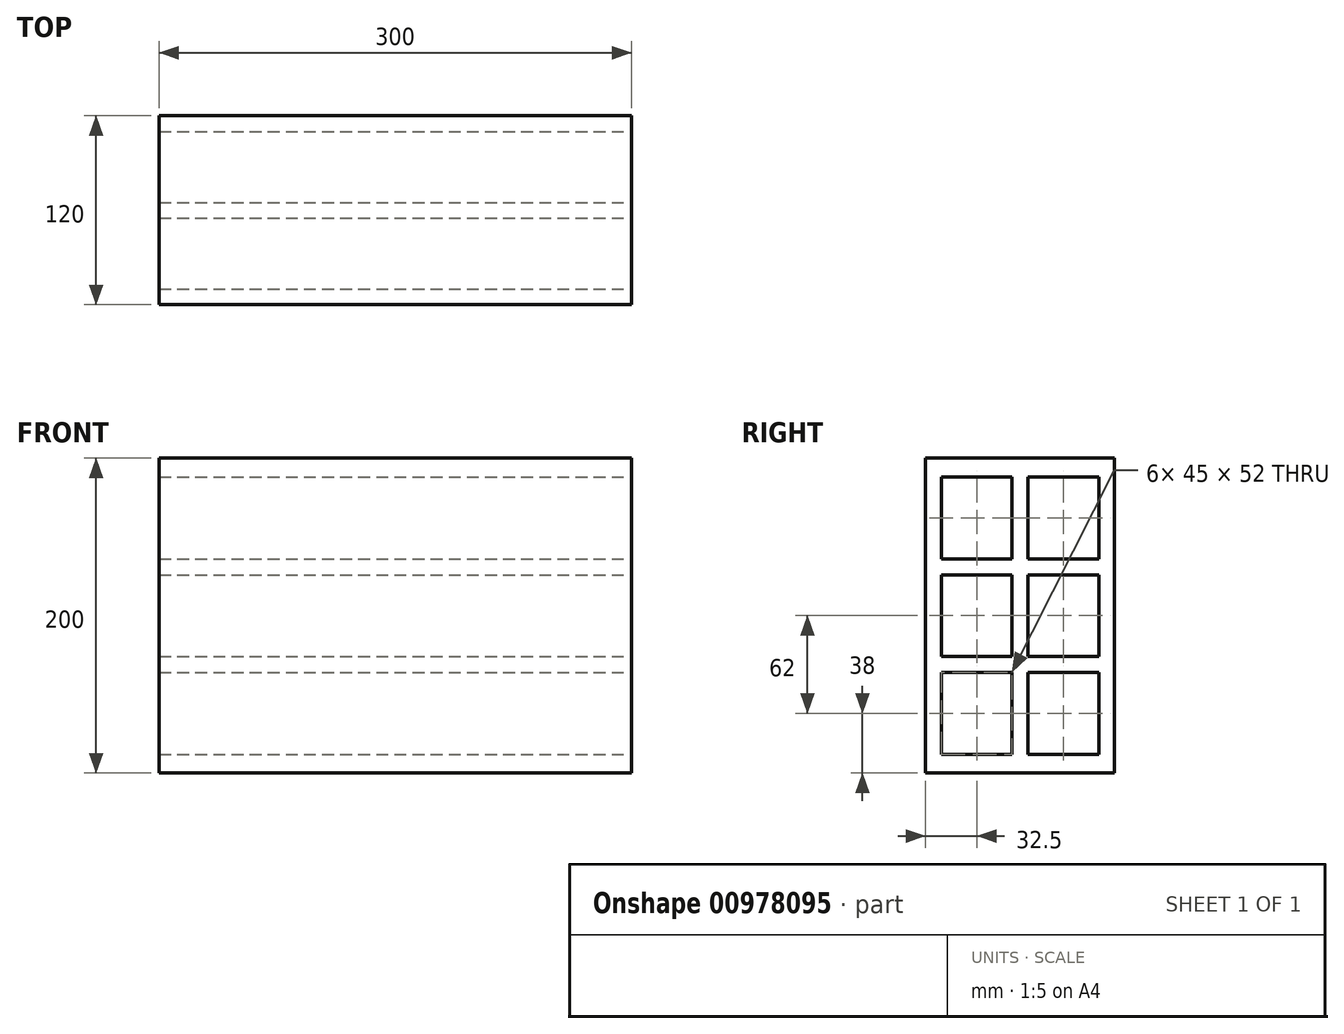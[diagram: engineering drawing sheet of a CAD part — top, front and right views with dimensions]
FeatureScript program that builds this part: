
annotation { "Feature Type Name" : "Feature", "Feature Type Description" : "" }
export const myFeature = defineFeature(function(context is Context, id is Id, definition is map)
    precondition{}
    {
        {
            var Q0;
            Q0=qCreatedBy(makeId("Front.planeOp"),FACE);
            var sketch = newSketch(context, id + "F0", { "sketchPlane" : qUnion([Q0])});
            skLineSegment(sketch, "E0.bottom", {"start": v(-150, 100) * mm, "end": v(150, 100) * mm});
            skLineSegment(sketch, "E0.top", {"start": v(-150, -100) * mm, "end": v(150, -100) * mm});
            skLineSegment(sketch, "E0.left", {"start": v(-150, 100) * mm, "end": v(-150, -100) * mm});
            skLineSegment(sketch, "E0.right", {"start": v(150, 100) * mm, "end": v(150, -100) * mm});
            skPoint(sketch, "E0.middle", {"position": v(0, 0) * mm});
            skSolve(sketch);
        }
        {
            var Q0;
            Q0=makeQuery(id+"F0.imprint","IMPRINT",FACE,{"disambiguationData":[TD([[makeQuery(id+"F0.imprint","IMPRINT",EDGE,{"derivedFrom":sQuery(id+"F0.wireOp",EDGE,"E0.bottom")}),-1.0]])]});
            extrude(context, id + "F1", {"entities" : qUnion([Q0]), "endBound" : BoundingType.SYMMETRIC, "depth" : 120 * mm, "offsetDistance" : 25 * mm});
        }
        {
            var Q0;
            Q0=makeQuery(id+"F1.opExtrude","SWEPT_FACE",FACE,{"disambiguationData":[OSD([sQuery(id+"F0.wireOp",EDGE,"E0.right")])]});
            var sketch = newSketch(context, id + "F2", { "sketchPlane" : qUnion([Q0])});
            skLineSegment(sketch, "E1.bottom", {"start": v(-50, 88) * mm, "end": v(-5, 88) * mm});
            skLineSegment(sketch, "E1.top", {"start": v(-50, -88) * mm, "end": v(-5, -88) * mm});
            skLineSegment(sketch, "E1.left", {"start": v(-50, 88) * mm, "end": v(-50, 36) * mm});
            skLineSegment(sketch, "E1.right", {"start": v(50, 88) * mm, "end": v(50, 36) * mm});
            skPoint(sketch, "E1.middle", {"position": v(0, 0) * mm});
            skLineSegment(sketch, "E2", {"start": v(-5, -88) * mm, "end": v(-5, -36) * mm});
            skLineSegment(sketch, "E3", {"start": v(5, 88) * mm, "end": v(5, 36) * mm});
            skLineSegment(sketch, "E4", {"start": v(-50, 36) * mm, "end": v(-5, 36) * mm});
            skLineSegment(sketch, "E5", {"start": v(-50, 26) * mm, "end": v(-5, 26) * mm});
            skLineSegment(sketch, "E6", {"start": v(5, 36) * mm, "end": v(50, 36) * mm});
            skLineSegment(sketch, "E7", {"start": v(50, 26) * mm, "end": v(5, 26) * mm});
            skLineSegment(sketch, "E8", {"start": v(-50, -26) * mm, "end": v(-5, -26) * mm});
            skLineSegment(sketch, "E9", {"start": v(50, -36) * mm, "end": v(5, -36) * mm});
            skLineSegment(sketch, "E10.trimOffspring", {"start": v(5, -26) * mm, "end": v(50, -26) * mm});
            skLineSegment(sketch, "E11.trimOffspring", {"start": v(-5, -36) * mm, "end": v(-50, -36) * mm});
            skLineSegment(sketch, "E12.trimOffspring", {"start": v(-5, 36) * mm, "end": v(-5, 88) * mm});
            skLineSegment(sketch, "E13.trimOffspring", {"start": v(5, 26) * mm, "end": v(5, -26) * mm});
            skLineSegment(sketch, "E14.trimOffspring", {"start": v(-5, -26) * mm, "end": v(-5, 26) * mm});
            skLineSegment(sketch, "E15.trimOffspring", {"start": v(5, -36) * mm, "end": v(5, -88) * mm});
            skLineSegment(sketch, "E16.trimOffspring", {"start": v(50, 26) * mm, "end": v(50, -26) * mm});
            skLineSegment(sketch, "E17.trimOffspring", {"start": v(50, -36) * mm, "end": v(50, -88) * mm});
            skLineSegment(sketch, "E18.trimOffspring", {"start": v(-50, -36) * mm, "end": v(-50, -88) * mm});
            skLineSegment(sketch, "E19.trimOffspring", {"start": v(-50, 26) * mm, "end": v(-50, -26) * mm});
            skLineSegment(sketch, "E20.trimOffspring", {"start": v(5, -88) * mm, "end": v(50, -88) * mm});
            skLineSegment(sketch, "E21.trimOffspring", {"start": v(5, 88) * mm, "end": v(50, 88) * mm});
            skSolve(sketch);
        }
        {
            var Q0;
            Q0 = qSketchRegion(id + "F2", true);
            extrude(context, id + "F3", {"entities" : qUnion([Q0]), "operationType" : NewBodyOperationType.REMOVE, "endBound" : BoundingType.UP_TO_NEXT, "oppositeDirection" : true, "depth" : 25 * mm, "offsetDistance" : 25 * mm});
        }
    });
